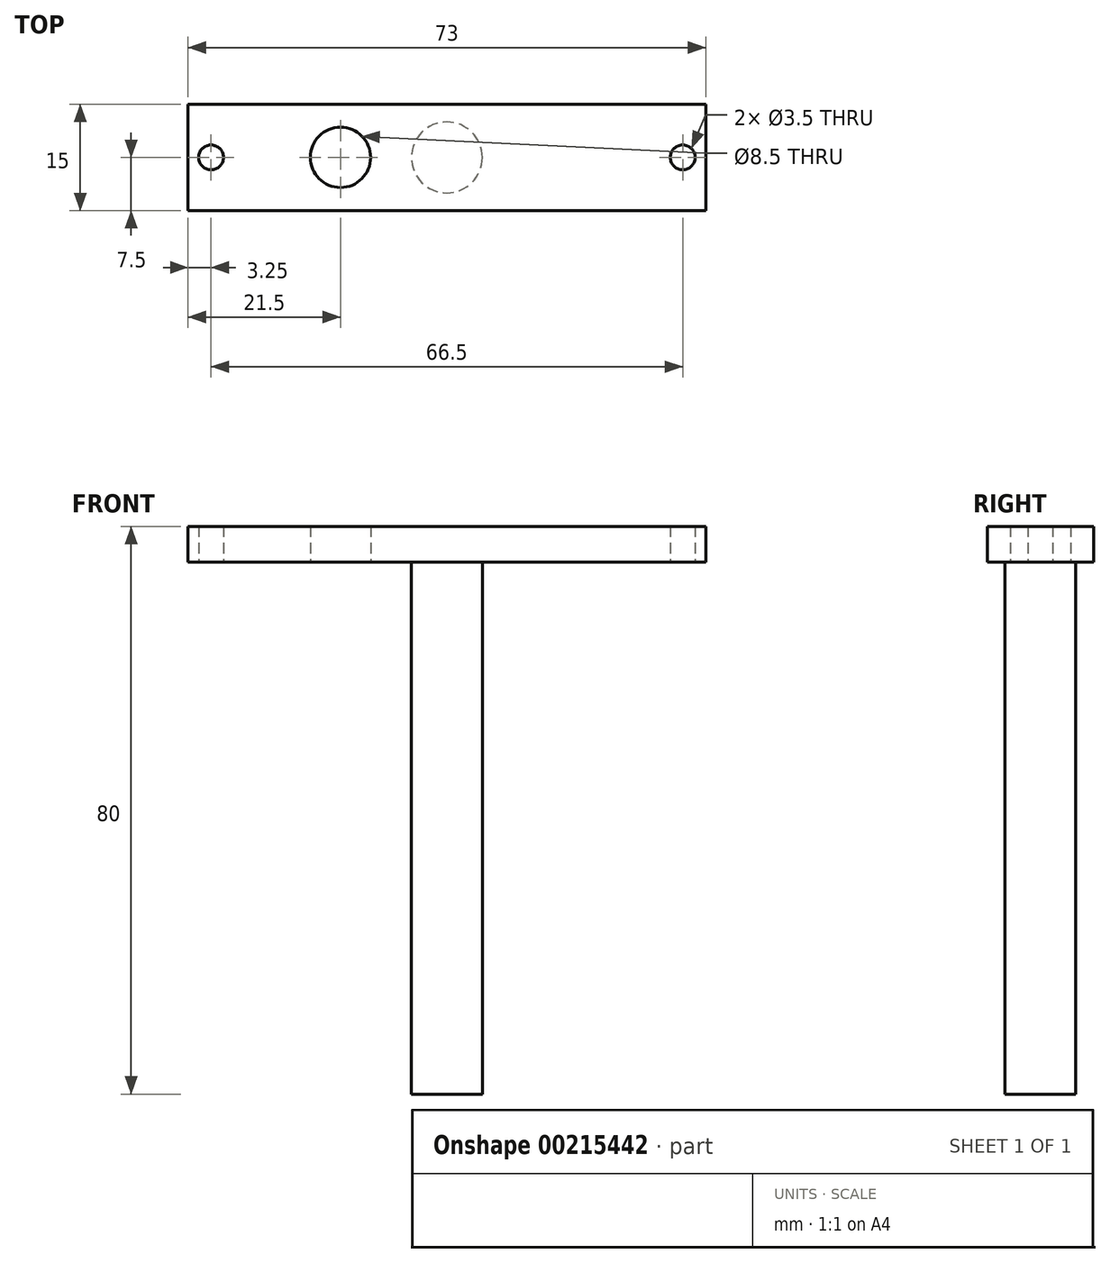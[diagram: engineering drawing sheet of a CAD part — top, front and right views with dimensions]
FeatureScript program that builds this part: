
annotation { "Feature Type Name" : "Feature", "Feature Type Description" : "" }
export const myFeature = defineFeature(function(context is Context, id is Id, definition is map)
    precondition{}
    {
        {
            var Q0;
            Q0=qCreatedBy(makeId("Top.planeOp"),FACE);
            var sketch = newSketch(context, id + "F0", { "sketchPlane" : qUnion([Q0])});
            skLineSegment(sketch, "E0.bottom", {"start": v(36.5, -7.5) * mm, "end": v(-36.5, -7.5) * mm});
            skLineSegment(sketch, "E0.top", {"start": v(36.5, 7.5) * mm, "end": v(-36.5, 7.5) * mm});
            skLineSegment(sketch, "E0.left", {"start": v(36.5, -7.5) * mm, "end": v(36.5, 7.5) * mm});
            skLineSegment(sketch, "E0.right", {"start": v(-36.5, -7.5) * mm, "end": v(-36.5, 7.5) * mm});
            skPoint(sketch, "E0.middle", {"position": v(0, 0) * mm});
            skCircle(sketch, "E1", {"center": v(-33.25, 0) * mm, "radius": 1.75 * mm});
            skCircle(sketch, "E2", {"center": v(33.25, 0) * mm, "radius": 1.75 * mm});
            skCircle(sketch, "E3", {"center": v(-15, 0) * mm, "radius": 4.25 * mm});
            skSolve(sketch);
        }
        {
            var Q0;
            Q0=makeQuery(id+"F0.imprint","IMPRINT",FACE,{"disambiguationData":[TD([[makeQuery(id+"F0.imprint","IMPRINT",EDGE,{"derivedFrom":sQuery(id+"F0.wireOp",EDGE,"E0.bottom")}),-1.0]])]});
            extrude(context, id + "F1", {"entities" : qUnion([Q0]), "depth" : 5 * mm});
        }
        {
            var Q0;
            Q0=makeQuery(id+"F1.opExtrude","CAP_FACE",FACE,{"disambiguationData":[OSD([sQuery(id+"F0.wireOp",EDGE,"E0.bottom"),sQuery(id+"F0.wireOp",EDGE,"E0.top"),sQuery(id+"F0.wireOp",EDGE,"E0.left"),sQuery(id+"F0.wireOp",EDGE,"E0.right"),sQuery(id+"F0.wireOp",EDGE,"E1"),sQuery(id+"F0.wireOp",EDGE,"E2"),sQuery(id+"F0.wireOp",EDGE,"E3")])],"isStart":true});
            var sketch = newSketch(context, id + "F2", { "sketchPlane" : qUnion([Q0])});
            skCircle(sketch, "E4", {"center": v(0, 0) * mm, "radius": 5 * mm});
            skSolve(sketch);
        }
        {
            var Q0;
            Q0=makeQuery(id+"F2.imprint","IMPRINT",FACE,{"disambiguationData":[TD([[makeQuery(id+"F2.imprint","IMPRINT",EDGE,{"derivedFrom":sQuery(id+"F2.wireOp",EDGE,"E4")}),1.0]])]});
            var Q1;
            Q1=sQuery(id+"F2.wireOp",EDGE,"E4");
            extrude(context, id + "F3", {"entities" : qUnion([Q0]), "operationType" : NewBodyOperationType.ADD, "surfaceEntities" : qUnion([Q1]), "depth" : 75 * mm});
        }
    });
